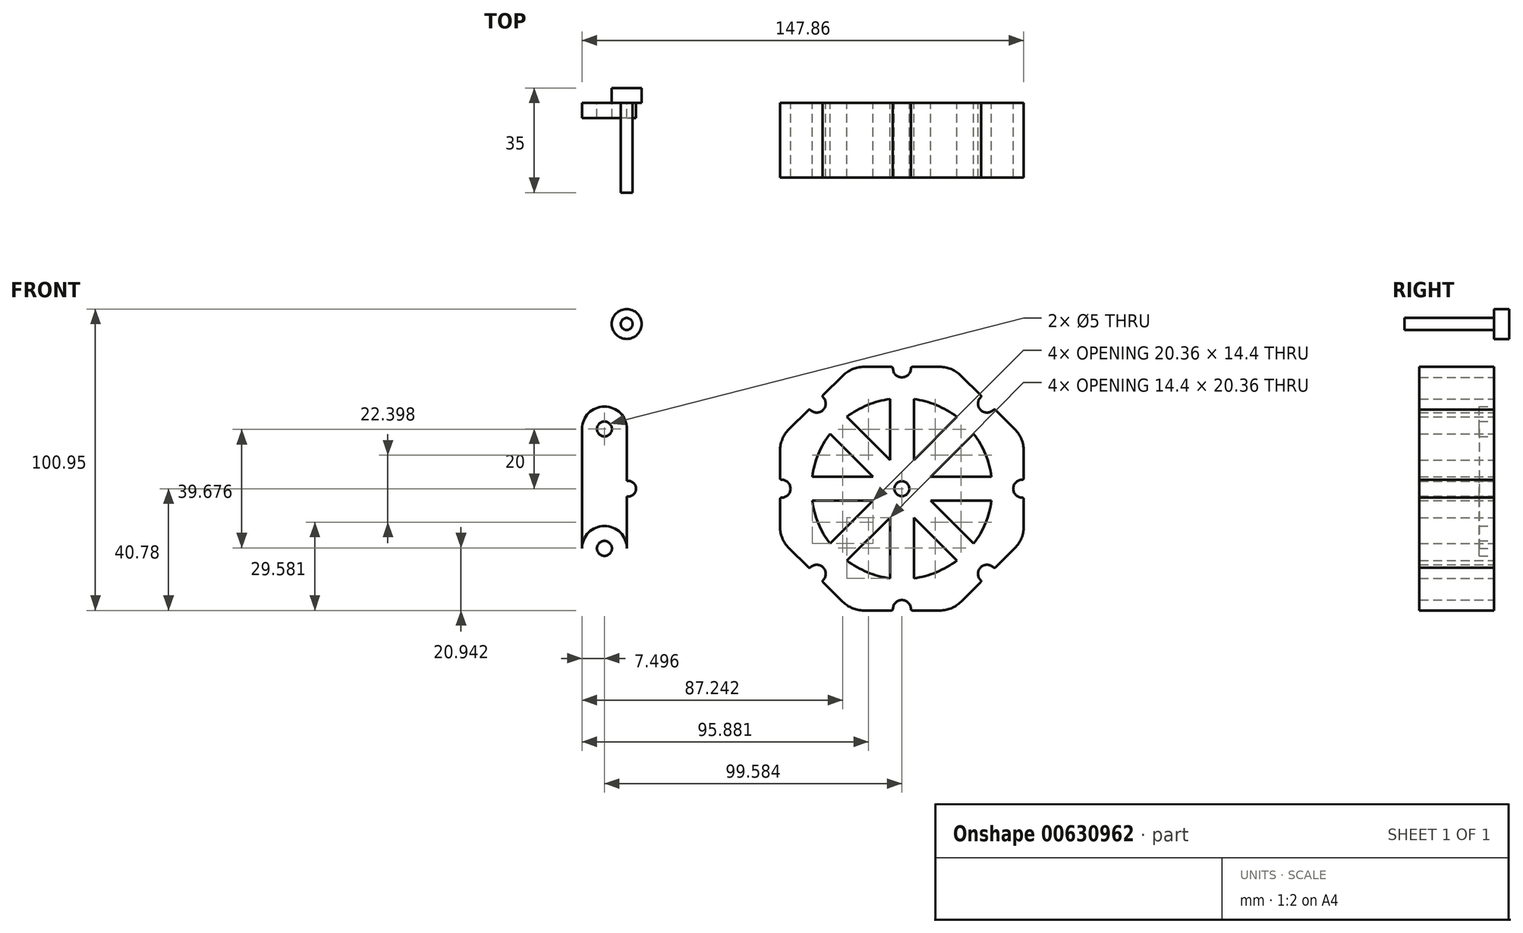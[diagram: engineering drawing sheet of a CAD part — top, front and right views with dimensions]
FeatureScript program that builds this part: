
annotation { "Feature Type Name" : "Feature", "Feature Type Description" : "" }
export const myFeature = defineFeature(function(context is Context, id is Id, definition is map)
    precondition{}
    {
        {
            var Q0;
            Q0=qCreatedBy(makeId("Front.planeOp"),FACE);
            var sketch = newSketch(context, id + "F0", { "sketchPlane" : qUnion([Q0])});
            skLineSegment(sketch, "E0.bottom", {"start": v(-107.08, 20) * mm, "end": v(-92.08, 20) * mm});
            skLineSegment(sketch, "E0.top", {"start": v(-107.08, 0) * mm, "end": v(-92.08, 0) * mm});
            skLineSegment(sketch, "E0.left", {"start": v(-107.08, 20) * mm, "end": v(-107.08, 0) * mm});
            skLineSegment(sketch, "E0.right", {"start": v(-92.08, 20) * mm, "end": v(-92.08, 0) * mm});
            skCircle(sketch, "E1", {"center": v(-99.58, 20) * mm, "radius": 7.5 * mm});
            skCircle(sketch, "E2", {"center": v(-99.58, 20) * mm, "radius": 2.5 * mm});
            skLineSegment(sketch, "E3.bottom", {"start": v(-92.08, 0) * mm, "end": v(-91.58, 0) * mm});
            skLineSegment(sketch, "E3.top", {"start": v(-92.08, 2.6) * mm, "end": v(-91.58, 2.6) * mm});
            skLineSegment(sketch, "E3.left", {"start": v(-92.08, 0) * mm, "end": v(-92.08, 2.6) * mm});
            skLineSegment(sketch, "E3.right", {"start": v(-91.58, 0) * mm, "end": v(-91.58, 2.6) * mm});
            skArc(sketch, "E4", {"start": v(-91.58, 2.6) * mm, "mid": v(-89.75, 1.84) * mm, "end": v(-88.98, 0) * mm});
            skLineSegment(sketch, "E5.MirrorCS", {"start": v(-107.08, -20) * mm, "end": v(-107.08, 0) * mm});
            skCircle(sketch, "E6.MirrorC", {"center": v(-99.58, -20) * mm, "radius": 7.5 * mm});
            skCircle(sketch, "E7.MirrorC", {"center": v(-99.58, -20) * mm, "radius": 2.5 * mm});
            skLineSegment(sketch, "E8.MirrorCS", {"start": v(-92.08, -20) * mm, "end": v(-92.08, 0) * mm});
            skLineSegment(sketch, "E9.MirrorCS", {"start": v(-92.08, -2.6) * mm, "end": v(-91.58, -2.6) * mm});
            skArc(sketch, "E10.MirrorCS", {"start": v(-91.58, -2.6) * mm, "mid": v(-89.75, -1.84) * mm, "end": v(-88.98, 0) * mm});
            skLineSegment(sketch, "E11", {"start": v(0, 0) * mm, "end": v(67.99, 0) * mm, "construction": true});
            skLineSegment(sketch, "E12", {"start": v(0, 0) * mm, "end": v(48.28, 20) * mm, "construction": true});
            skLineSegment(sketch, "E13", {"start": v(0, 0) * mm, "end": v(48.28, -20) * mm, "construction": true});
            skLineSegment(sketch, "E14", {"start": v(48.28, -20) * mm, "end": v(48.28, 0) * mm, "construction": true});
            skLineSegment(sketch, "E15", {"start": v(48.28, 20) * mm, "end": v(48.28, 0) * mm, "construction": true});
            skLineSegment(sketch, "E16", {"start": v(40.78, -3.5) * mm, "end": v(40.78, -16.9) * mm});
            skLineSegment(sketch, "E17.bottom", {"start": v(40.28, 3) * mm, "end": v(40.28, 3) * mm});
            skLineSegment(sketch, "E17.top", {"start": v(40.28, -3) * mm, "end": v(40.28, -3) * mm});
            skLineSegment(sketch, "E17.left", {"start": v(40.28, 3) * mm, "end": v(40.28, -3) * mm, "construction": true});
            skArc(sketch, "E18", {"start": v(40.28, 3) * mm, "mid": v(37.28, 0) * mm, "end": v(40.28, -3) * mm});
            skPoint(sketch, "E19.newPointB", {"position": v(40.78, 16.9) * mm});
            skArc(sketch, "E19.filletArc", {"start": v(40.78, -3.5) * mm, "mid": v(40.64, -3.15) * mm, "end": v(40.28, -3) * mm});
            skLineSegment(sketch, "E20", {"start": v(40.78, 16.9) * mm, "end": v(40.78, 3.5) * mm});
            skArc(sketch, "E21.filletArc", {"start": v(40.28, 3) * mm, "mid": v(40.64, 3.15) * mm, "end": v(40.78, 3.5) * mm});
            skLineSegment(sketch, "E22", {"start": v(40.78, 3.5) * mm, "end": v(40.78, -3.5) * mm, "construction": true});
            skArc(sketch, "E23", {"start": v(40.78, -12.75) * mm, "mid": v(40.6, -14.7) * mm, "end": v(40.02, -16.58) * mm});
            skArc(sketch, "E24", {"start": v(40.78, 12.75) * mm, "mid": v(40.6, 14.7) * mm, "end": v(40.02, 16.58) * mm});
            skCircle(sketch, "E25", {"center": v(0, 0) * mm, "radius": 9 * mm, "construction": true});
            skCircle(sketch, "E26", {"center": v(0, 0) * mm, "radius": 30.28 * mm});
            skLineSegment(sketch, "E27", {"start": v(8.06, -4) * mm, "end": v(30.02, -4) * mm});
            skLineSegment(sketch, "E28", {"start": v(8.06, 4) * mm, "end": v(30.02, 4) * mm});
            skCircle(sketch, "E29", {"center": v(0, 0) * mm, "radius": 40.28 * mm, "construction": true});
            skLineSegment(sketch, "E30", {"start": v(23.64, 0) * mm, "end": v(23.64, 4) * mm, "construction": true});
            skLineSegment(sketch, "E31", {"start": v(23.64, 0) * mm, "end": v(23.64, -4) * mm, "construction": true});
            skLineSegment(sketch, "E32.1.0", {"start": v(2.87, 8.53) * mm, "end": v(18.4, 24.06) * mm});
            skLineSegment(sketch, "E32.1.1", {"start": v(8.53, 2.87) * mm, "end": v(24.06, 18.4) * mm});
            skArc(sketch, "E32.1.2", {"start": v(19.82, 37.86) * mm, "mid": v(18.3, 39.1) * mm, "end": v(16.58, 40.02) * mm});
            skLineSegment(sketch, "E32.1.3", {"start": v(16.9, 40.78) * mm, "end": v(26.36, 31.31) * mm});
            skArc(sketch, "E32.1.4", {"start": v(26.36, 30.6) * mm, "mid": v(26.51, 30.96) * mm, "end": v(26.36, 31.31) * mm});
            skArc(sketch, "E32.1.5", {"start": v(26.36, 30.6) * mm, "mid": v(26.36, 26.36) * mm, "end": v(30.6, 26.36) * mm});
            skArc(sketch, "E32.1.6", {"start": v(31.31, 26.36) * mm, "mid": v(30.96, 26.51) * mm, "end": v(30.6, 26.36) * mm});
            skLineSegment(sketch, "E32.1.7", {"start": v(31.31, 26.36) * mm, "end": v(40.78, 16.9) * mm});
            skArc(sketch, "E32.1.8", {"start": v(37.86, 19.82) * mm, "mid": v(39.1, 18.3) * mm, "end": v(40.02, 16.58) * mm});
            skLineSegment(sketch, "E32.2.0", {"start": v(-4, 8.06) * mm, "end": v(-4, 30.02) * mm});
            skLineSegment(sketch, "E32.2.1", {"start": v(4, 8.06) * mm, "end": v(4, 30.02) * mm});
            skArc(sketch, "E32.2.2", {"start": v(-12.75, 40.78) * mm, "mid": v(-14.7, 40.6) * mm, "end": v(-16.58, 40.02) * mm});
            skLineSegment(sketch, "E32.2.3", {"start": v(-16.9, 40.78) * mm, "end": v(-3.5, 40.78) * mm});
            skArc(sketch, "E32.2.4", {"start": v(-3, 40.28) * mm, "mid": v(-3.15, 40.64) * mm, "end": v(-3.5, 40.78) * mm});
            skArc(sketch, "E32.2.5", {"start": v(-3, 40.28) * mm, "mid": v(0, 37.28) * mm, "end": v(3, 40.28) * mm});
            skArc(sketch, "E32.2.6", {"start": v(3.5, 40.78) * mm, "mid": v(3.15, 40.64) * mm, "end": v(3, 40.28) * mm});
            skLineSegment(sketch, "E32.2.7", {"start": v(3.5, 40.78) * mm, "end": v(16.9, 40.78) * mm});
            skArc(sketch, "E32.2.8", {"start": v(12.75, 40.78) * mm, "mid": v(14.7, 40.6) * mm, "end": v(16.58, 40.02) * mm});
            skLineSegment(sketch, "E32.3.0", {"start": v(-8.53, 2.87) * mm, "end": v(-24.06, 18.4) * mm});
            skLineSegment(sketch, "E32.3.1", {"start": v(-2.87, 8.53) * mm, "end": v(-18.4, 24.06) * mm});
            skArc(sketch, "E32.3.2", {"start": v(-37.86, 19.82) * mm, "mid": v(-39.1, 18.3) * mm, "end": v(-40.02, 16.58) * mm});
            skLineSegment(sketch, "E32.3.3", {"start": v(-40.78, 16.9) * mm, "end": v(-31.31, 26.36) * mm});
            skArc(sketch, "E32.3.4", {"start": v(-30.6, 26.36) * mm, "mid": v(-30.96, 26.51) * mm, "end": v(-31.31, 26.36) * mm});
            skArc(sketch, "E32.3.5", {"start": v(-30.6, 26.36) * mm, "mid": v(-26.36, 26.36) * mm, "end": v(-26.36, 30.6) * mm});
            skArc(sketch, "E32.3.6", {"start": v(-26.36, 31.31) * mm, "mid": v(-26.51, 30.96) * mm, "end": v(-26.36, 30.6) * mm});
            skLineSegment(sketch, "E32.3.7", {"start": v(-26.36, 31.31) * mm, "end": v(-16.9, 40.78) * mm});
            skArc(sketch, "E32.3.8", {"start": v(-19.82, 37.86) * mm, "mid": v(-18.3, 39.1) * mm, "end": v(-16.58, 40.02) * mm});
            skLineSegment(sketch, "E32.4.0", {"start": v(-8.06, -4) * mm, "end": v(-30.02, -4) * mm});
            skLineSegment(sketch, "E32.4.1", {"start": v(-8.06, 4) * mm, "end": v(-30.02, 4) * mm});
            skArc(sketch, "E32.4.2", {"start": v(-40.78, -12.75) * mm, "mid": v(-40.6, -14.7) * mm, "end": v(-40.02, -16.58) * mm});
            skLineSegment(sketch, "E32.4.3", {"start": v(-40.78, -16.9) * mm, "end": v(-40.78, -3.5) * mm});
            skArc(sketch, "E32.4.4", {"start": v(-40.28, -3) * mm, "mid": v(-40.64, -3.15) * mm, "end": v(-40.78, -3.5) * mm});
            skArc(sketch, "E32.4.5", {"start": v(-40.28, -3) * mm, "mid": v(-37.28, 0) * mm, "end": v(-40.28, 3) * mm});
            skArc(sketch, "E32.4.6", {"start": v(-40.78, 3.5) * mm, "mid": v(-40.64, 3.15) * mm, "end": v(-40.28, 3) * mm});
            skLineSegment(sketch, "E32.4.7", {"start": v(-40.78, 3.5) * mm, "end": v(-40.78, 16.9) * mm});
            skArc(sketch, "E32.4.8", {"start": v(-40.78, 12.75) * mm, "mid": v(-40.6, 14.7) * mm, "end": v(-40.02, 16.58) * mm});
            skLineSegment(sketch, "E32.5.0", {"start": v(-2.87, -8.53) * mm, "end": v(-18.4, -24.06) * mm});
            skLineSegment(sketch, "E32.5.1", {"start": v(-8.53, -2.87) * mm, "end": v(-24.06, -18.4) * mm});
            skArc(sketch, "E32.5.2", {"start": v(-19.82, -37.86) * mm, "mid": v(-18.3, -39.1) * mm, "end": v(-16.58, -40.02) * mm});
            skLineSegment(sketch, "E32.5.3", {"start": v(-16.9, -40.78) * mm, "end": v(-26.36, -31.31) * mm});
            skArc(sketch, "E32.5.4", {"start": v(-26.36, -30.6) * mm, "mid": v(-26.51, -30.96) * mm, "end": v(-26.36, -31.31) * mm});
            skArc(sketch, "E32.5.5", {"start": v(-26.36, -30.6) * mm, "mid": v(-26.36, -26.36) * mm, "end": v(-30.6, -26.36) * mm});
            skArc(sketch, "E32.5.6", {"start": v(-31.31, -26.36) * mm, "mid": v(-30.96, -26.51) * mm, "end": v(-30.6, -26.36) * mm});
            skLineSegment(sketch, "E32.5.7", {"start": v(-31.31, -26.36) * mm, "end": v(-40.78, -16.9) * mm});
            skArc(sketch, "E32.5.8", {"start": v(-37.86, -19.82) * mm, "mid": v(-39.1, -18.3) * mm, "end": v(-40.02, -16.58) * mm});
            skLineSegment(sketch, "E32.6.0", {"start": v(4, -8.06) * mm, "end": v(4, -30.02) * mm});
            skLineSegment(sketch, "E32.6.1", {"start": v(-4, -8.06) * mm, "end": v(-4, -30.02) * mm});
            skArc(sketch, "E32.6.2", {"start": v(12.75, -40.78) * mm, "mid": v(14.7, -40.6) * mm, "end": v(16.58, -40.02) * mm});
            skLineSegment(sketch, "E32.6.3", {"start": v(16.9, -40.78) * mm, "end": v(3.5, -40.78) * mm});
            skArc(sketch, "E32.6.4", {"start": v(3, -40.28) * mm, "mid": v(3.15, -40.64) * mm, "end": v(3.5, -40.78) * mm});
            skArc(sketch, "E32.6.5", {"start": v(3, -40.28) * mm, "mid": v(0, -37.28) * mm, "end": v(-3, -40.28) * mm});
            skArc(sketch, "E32.6.6", {"start": v(-3.5, -40.78) * mm, "mid": v(-3.15, -40.64) * mm, "end": v(-3, -40.28) * mm});
            skLineSegment(sketch, "E32.6.7", {"start": v(-3.5, -40.78) * mm, "end": v(-16.9, -40.78) * mm});
            skArc(sketch, "E32.6.8", {"start": v(-12.75, -40.78) * mm, "mid": v(-14.7, -40.6) * mm, "end": v(-16.58, -40.02) * mm});
            skLineSegment(sketch, "E32.7.0", {"start": v(8.53, -2.87) * mm, "end": v(24.06, -18.4) * mm});
            skLineSegment(sketch, "E32.7.1", {"start": v(2.87, -8.53) * mm, "end": v(18.4, -24.06) * mm});
            skArc(sketch, "E32.7.2", {"start": v(37.86, -19.82) * mm, "mid": v(39.1, -18.3) * mm, "end": v(40.02, -16.58) * mm});
            skLineSegment(sketch, "E32.7.3", {"start": v(40.78, -16.9) * mm, "end": v(31.31, -26.36) * mm});
            skArc(sketch, "E32.7.4", {"start": v(30.6, -26.36) * mm, "mid": v(30.96, -26.51) * mm, "end": v(31.31, -26.36) * mm});
            skArc(sketch, "E32.7.5", {"start": v(30.6, -26.36) * mm, "mid": v(26.36, -26.36) * mm, "end": v(26.36, -30.6) * mm});
            skArc(sketch, "E32.7.6", {"start": v(26.36, -31.31) * mm, "mid": v(26.51, -30.96) * mm, "end": v(26.36, -30.6) * mm});
            skLineSegment(sketch, "E32.7.7", {"start": v(26.36, -31.31) * mm, "end": v(16.9, -40.78) * mm});
            skArc(sketch, "E32.7.8", {"start": v(19.82, -37.86) * mm, "mid": v(18.3, -39.1) * mm, "end": v(16.58, -40.02) * mm});
            skCircle(sketch, "E33", {"center": v(0, 0) * mm, "radius": 2.5 * mm});
            skCircle(sketch, "E34", {"center": v(-92.14, 55.17) * mm, "radius": 2 * mm});
            skCircle(sketch, "E35", {"center": v(-92.14, 55.17) * mm, "radius": 5 * mm});
            skSolve(sketch);
        }
        {
            var Q0;
            Q0=makeQuery(id+"F0.imprint","IMPRINT",FACE,{"disambiguationData":[TD([[makeQuery(id+"F0.imprint","IMPRINT",EDGE,{"derivedFrom":sQuery(id+"F0.wireOp",EDGE,"E0.top")}),1.0]])]});
            var Q1;
            {var subQ5=sQuery(id+"F0.wireOp",EDGE,"E0.top");Q1=makeQuery(id+"F0.imprint","IMPRINT",FACE,{"disambiguationData":[TD([[makeQuery(id+"F0.imprint","IMPRINT",EDGE,{"derivedFrom":subQ5}),-1.0]])]});}
            var Q2;
            {var subQ1=sQuery(id+"F0.wireOp",EDGE,"E0.bottom");var subQ3=sQuery(id+"F0.wireOp",EDGE,"E2");var subQ4=makeQuery(id+"F0.imprint","INTERSECT",VERTEX,{"disambiguationData":[OD(0.0)],"derivedFrom":[subQ1,subQ3]});Q2=makeQuery(id+"F0.imprint","IMPRINT",FACE,{"disambiguationData":[TD([[makeQuery(id+"F0.imprint","IMPRINT",EDGE,{"disambiguationData":[TD([[subQ4,-1.0]])],"derivedFrom":subQ3}),-1.0]])]});}
            var Q3;
            {var subQ1=sQuery(id+"F0.wireOp",EDGE,"E0.bottom");var subQ3=sQuery(id+"F0.wireOp",EDGE,"E2");var subQ4=makeQuery(id+"F0.imprint","INTERSECT",VERTEX,{"disambiguationData":[OD(0.0)],"derivedFrom":[subQ1,subQ3]});Q3=makeQuery(id+"F0.imprint","IMPRINT",FACE,{"disambiguationData":[TD([[makeQuery(id+"F0.imprint","IMPRINT",EDGE,{"disambiguationData":[TD([[subQ4,1.0]])],"derivedFrom":subQ3}),-1.0]])]});}
            var Q4;
            {var subQ1=sQuery(id+"F0.wireOp",EDGE,"E3.bottom");Q4=makeQuery(id+"F0.imprint","IMPRINT",FACE,{"disambiguationData":[TD([[makeQuery(id+"F0.imprint","IMPRINT",EDGE,{"derivedFrom":subQ1}),-1.0]])]});}
            var Q5;
            Q5=makeQuery(id+"F0.imprint","IMPRINT",FACE,{"disambiguationData":[TD([[makeQuery(id+"F0.imprint","IMPRINT",EDGE,{"derivedFrom":sQuery(id+"F0.wireOp",EDGE,"E3.bottom")}),1.0]])]});
            var Q6;
            Q6=makeQuery(id+"F0.imprint","IMPRINT",FACE,{"disambiguationData":[TD([[makeQuery(id+"F0.imprint","IMPRINT",EDGE,{"derivedFrom":sQuery(id+"F0.wireOp",EDGE,"E7.MirrorC")}),1.0]])]});
            extrude(context, id + "F1", {"entities" : qUnion([Q0, Q1, Q2, Q3, Q4, Q5, Q6]), "depth" : 5 * mm, "offsetDistance" : 25 * mm});
        }
        {
            var Q0;
            Q0=makeQuery(id+"F0.imprint","IMPRINT",FACE,{"disambiguationData":[TD([[makeQuery(id+"F0.imprint","IMPRINT",EDGE,{"derivedFrom":sQuery(id+"F0.wireOp",EDGE,"E33")}),-1.0]])]});
            var Q1;
            Q1=makeQuery(id+"F0.imprint","IMPRINT",FACE,{"disambiguationData":[TD([[makeQuery(id+"F0.imprint","IMPRINT",EDGE,{"derivedFrom":sQuery(id+"F0.wireOp",EDGE,"E18")}),-1.0]])]});
            extrude(context, id + "F2", {"entities" : qUnion([Q0, Q1]), "depth" : 25 * mm, "offsetDistance" : 25 * mm});
        }
        {
            var Q0;
            Q0=makeQuery(id+"F0.imprint","IMPRINT",FACE,{"disambiguationData":[TD([[makeQuery(id+"F0.imprint","IMPRINT",EDGE,{"derivedFrom":sQuery(id+"F0.wireOp",EDGE,"E34")}),1.0]])]});
            extrude(context, id + "F3", {"entities" : qUnion([Q0]), "depth" : 30 * mm, "offsetDistance" : 25 * mm});
        }
        {
            var Q0;
            Q0=makeQuery(id+"F0.imprint","IMPRINT",FACE,{"disambiguationData":[TD([[makeQuery(id+"F0.imprint","IMPRINT",EDGE,{"derivedFrom":sQuery(id+"F0.wireOp",EDGE,"E34")}),-1.0]])]});
            var Q1;
            Q1=makeQuery(id+"F0.imprint","IMPRINT",FACE,{"disambiguationData":[TD([[makeQuery(id+"F0.imprint","IMPRINT",EDGE,{"derivedFrom":sQuery(id+"F0.wireOp",EDGE,"E34")}),1.0]])]});
            extrude(context, id + "F4", {"entities" : qUnion([Q0, Q1]), "operationType" : NewBodyOperationType.ADD, "oppositeDirection" : true, "depth" : 5 * mm, "offsetDistance" : 25 * mm});
        }
    });
